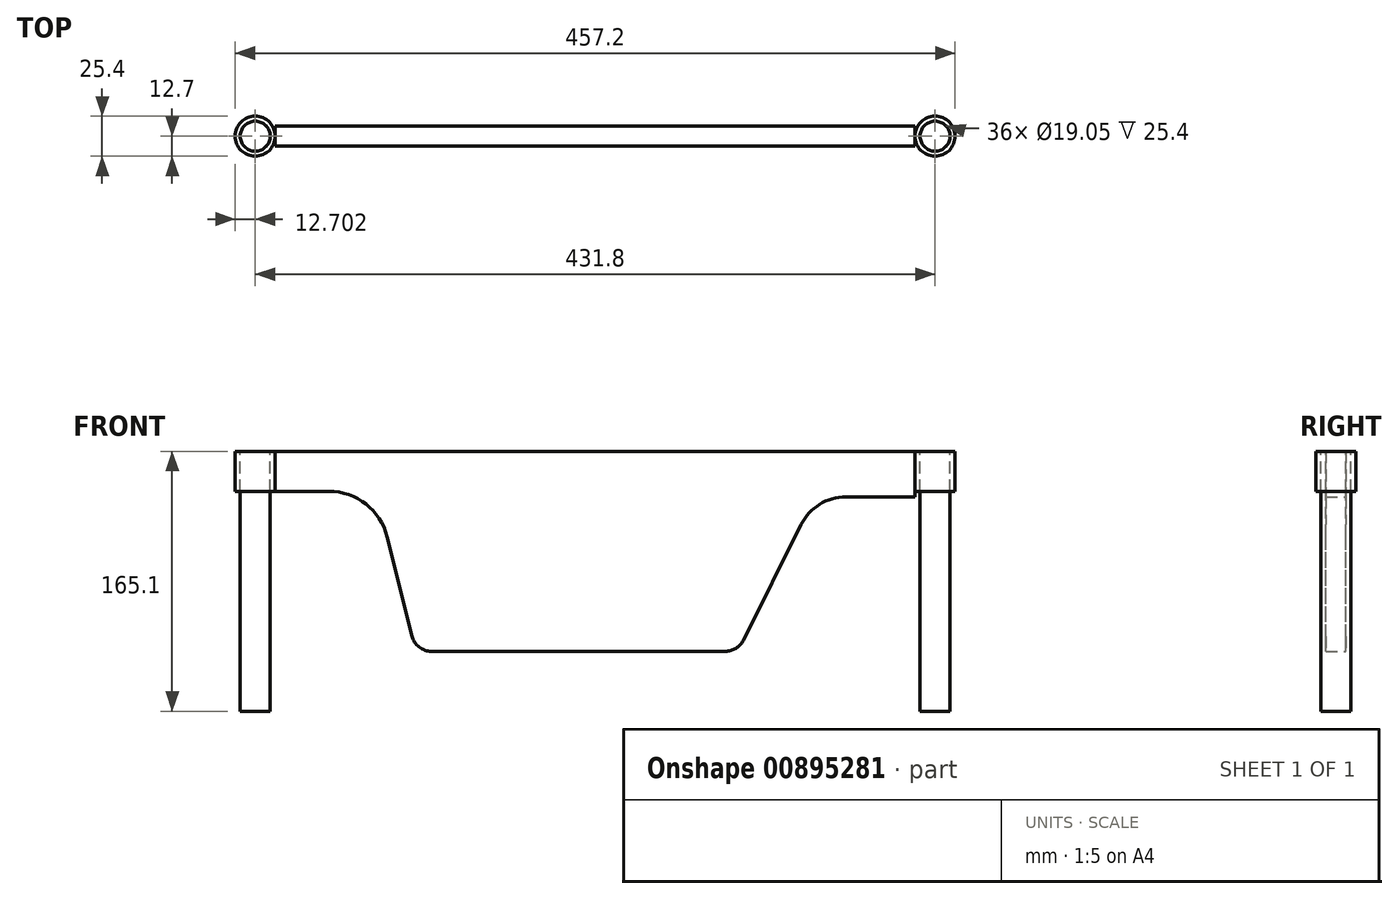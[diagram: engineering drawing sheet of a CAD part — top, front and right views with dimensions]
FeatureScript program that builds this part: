
annotation { "Feature Type Name" : "Feature", "Feature Type Description" : "" }
export const myFeature = defineFeature(function(context is Context, id is Id, definition is map)
    precondition{}
    {
        {
            var Q0;
            Q0=qCreatedBy(makeId("Front.planeOp"),FACE);
            var sketch = newSketch(context, id + "F0", { "sketchPlane" : qUnion([Q0])});
            skLineSegment(sketch, "E0.0", {"start": v(-487.35, 149.87) * mm, "end": v(-521.5, 149.87) * mm});
            skArc(sketch, "E0.1", {"start": v(-487.35, 149.87) * mm, "mid": v(-463.9, 141.8) * mm, "end": v(-450.4, 121) * mm});
            skLineSegment(sketch, "E0.2", {"start": v(-434.61, 57.89) * mm, "end": v(-450.4, 121) * mm});
            skArc(sketch, "E0.3", {"start": v(-422.3, 48.27) * mm, "mid": v(-430.1, 50.96) * mm, "end": v(-434.61, 57.89) * mm});
            skLineSegment(sketch, "E0.4", {"start": v(-422.3, 48.27) * mm, "end": v(-235.57, 48.27) * mm});
            skLineSegment(sketch, "E0.5", {"start": v(-159.05, 146.36) * mm, "end": v(-115.1, 146.36) * mm});
            skArc(sketch, "E0.6", {"start": v(-187.45, 128.8) * mm, "mid": v(-175.75, 141.62) * mm, "end": v(-159.05, 146.36) * mm});
            skLineSegment(sketch, "E0.7", {"start": v(-224.21, 55.29) * mm, "end": v(-187.45, 128.8) * mm});
            skArc(sketch, "E0.8", {"start": v(-224.21, 55.29) * mm, "mid": v(-228.9, 50.16) * mm, "end": v(-235.57, 48.27) * mm});
            skLineSegment(sketch, "E1", {"start": v(-521.5, 149.87) * mm, "end": v(-521.5, 175.27) * mm});
            skLineSegment(sketch, "E2", {"start": v(-115.1, 175.27) * mm, "end": v(-115.1, 146.36) * mm});
            skLineSegment(sketch, "E3", {"start": v(-521.5, 175.27) * mm, "end": v(-115.1, 175.27) * mm});
            skSolve(sketch);
        }
        {
            var Q0;
            Q0 = qSketchRegion(id + "F0", true);
            extrude(context, id + "F1", {"entities" : qUnion([Q0]), "depth" : 12.7 * mm, "offsetDistance" : 25.4 * mm});
        }
        {
            var Q0;
            Q0=makeQuery(id+"F1.opExtrude","SWEPT_FACE",FACE,{"disambiguationData":[OSD([sQuery(id+"F0.wireOp",EDGE,"E3")])]});
            var sketch = newSketch(context, id + "F2", { "sketchPlane" : qUnion([Q0])});
            skCircle(sketch, "E4", {"center": v(-102.4, -6.35) * mm, "radius": 9.53 * mm});
            skPoint(sketch, "E4.centerSnap0", {"position": v(-115.1, -6.35) * mm});
            skCircle(sketch, "E5", {"center": v(-102.4, -6.35) * mm, "radius": 12.7 * mm});
            skCircle(sketch, "E6", {"center": v(-534.2, -6.35) * mm, "radius": 9.53 * mm});
            skPoint(sketch, "E6.centerSnap0", {"position": v(-521.5, -6.35) * mm});
            skCircle(sketch, "E7", {"center": v(-534.2, -6.35) * mm, "radius": 12.7 * mm});
            skSolve(sketch);
        }
        {
            var Q0;
            Q0 = qSketchRegion(id + "F2", true);
            extrude(context, id + "F3", {"entities" : qUnion([Q0]), "oppositeDirection" : true, "depth" : 25.4 * mm, "offsetDistance" : 25.4 * mm});
        }
        {
            var Q0;
            Q0=makeQuery(id+"F1.opExtrude","SWEPT_FACE",FACE,{"disambiguationData":[OSD([sQuery(id+"F0.wireOp",EDGE,"E3")])]});
            var sketch = newSketch(context, id + "F4", { "sketchPlane" : qUnion([Q0])});
            skCircle(sketch, "E8", {"center": v(-102.4, -6.35) * mm, "radius": 9.51 * mm});
            skPoint(sketch, "E8.centerSnap0", {"position": v(-115.1, -6.35) * mm});
            skCircle(sketch, "E9", {"center": v(-534.2, -6.35) * mm, "radius": 9.51 * mm});
            skSolve(sketch);
        }
        {
            var Q0;
            Q0 = qSketchRegion(id + "F4", true);
            extrude(context, id + "F5", {"entities" : qUnion([Q0]), "oppositeDirection" : true, "depth" : 165.1 * mm, "offsetDistance" : 25.4 * mm});
        }
    });
